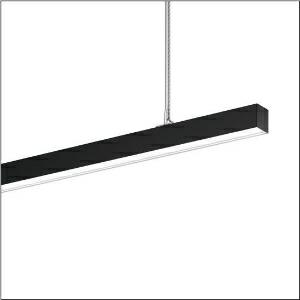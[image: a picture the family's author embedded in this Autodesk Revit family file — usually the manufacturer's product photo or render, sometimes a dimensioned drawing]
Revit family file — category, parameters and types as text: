
# Revit family: silica_21_51mx33dc4dbb
name_source: partatom
category: Lighting Fixtures
units: mm (PartAtom-declared; Revit-internal decimal feet)

## family parameters
Cut with Voids When Loaded = No
Host = Face
Light Source = No
Part Type = Normal
Room Calculation Point = No
Round Connector Dimension = Use Diameter
Shared = No

## types (1)
- --- (1 x LED, 14790 lm, 93.9 W, 4000K)
    Apparent Load = 94 VA
    CIE Flux Codes = 78 96 99 55 100
    Color Rendering = 80
    Color Temperature = 4000K
    Default Elevation = 1800 mm
    Description = Silica 21, office luminaire, primary optical cover: prismatic diffuser, of PMMA, CAT 2 (L<= 3000cd/m²), light emission: direct/indirect distribution, primary light characteristic: symmetric, installation type: suspended mounting, LED, rated luminous flux: 14.790lm, luminous efficacy: 158lm/W, light colour: 840, colour temperature: 4000K, control gear: DALI 2, with terminal, 3+2-pole, max. 2.5mm², mains connection: 220..240V, AC, 50/60Hz, rated input power: 93.9W, luminaire housing, of aluminium, matt jet black (RAL 9005), length: 3.004mm, width: 53mm, height: 53mm, protection rating (complete): IP20, insulation class (complete): insulation class I (protective earthing), certification: CE, permissible operating ambient temperature: 0..+35°C, standard: EN 50419, packaging unit: 1 piece
    Height = 53 mm
    Lamp = 1 x LED
    Lamp Light Flux = 14790 lm
    Lamp Power = 93.9 W
    Lamp count = 1
    Length = 3004 mm
    Luminous efficacy = 158 lm/W
    Manufacturer = Siteco
    ModVariant = No
    Model = 51MX33DC4DBB
    Mounting Place = Ceiling
    Mounting Type = Pendant
    Number of Poles = 1
    OnlyDefault = Yes
    Power Factor = 1
    Product Name = Silica 21
    Product group = office luminaire | ceiling pendant
    ProductGroupID = 903
    Protection Class = Protection class I
    Protection Degree = IP 20
    RLX_Detail_Level = 1
    RLX_Emergency_Light_Flux = 0 lm
    RLX_Emergency_Type = 0
    RLX_Emergency_Type_DB = No
    RlxData = <blob elided: 26133 chars, md5=3d63b3aa>
    Socket = socket
    Standby Power = 0 W
    System Light Flux = 14790 lm
    System Power = 94 W
    Type Comments = factory setting: luminous flux: 100 % | dim-lin: 254 | 323 mA
    Type Image = l_1335856.jpg
    URL = http://relux.com
    VarID = @adj_118837
    Voltage = 0 V
    Weight = 0.00 kg
    Width = 53 mm

## geometry (parser evidence)
native form markers: Blend x4, Sweep x15
no freeform markers — native parametric forms only
